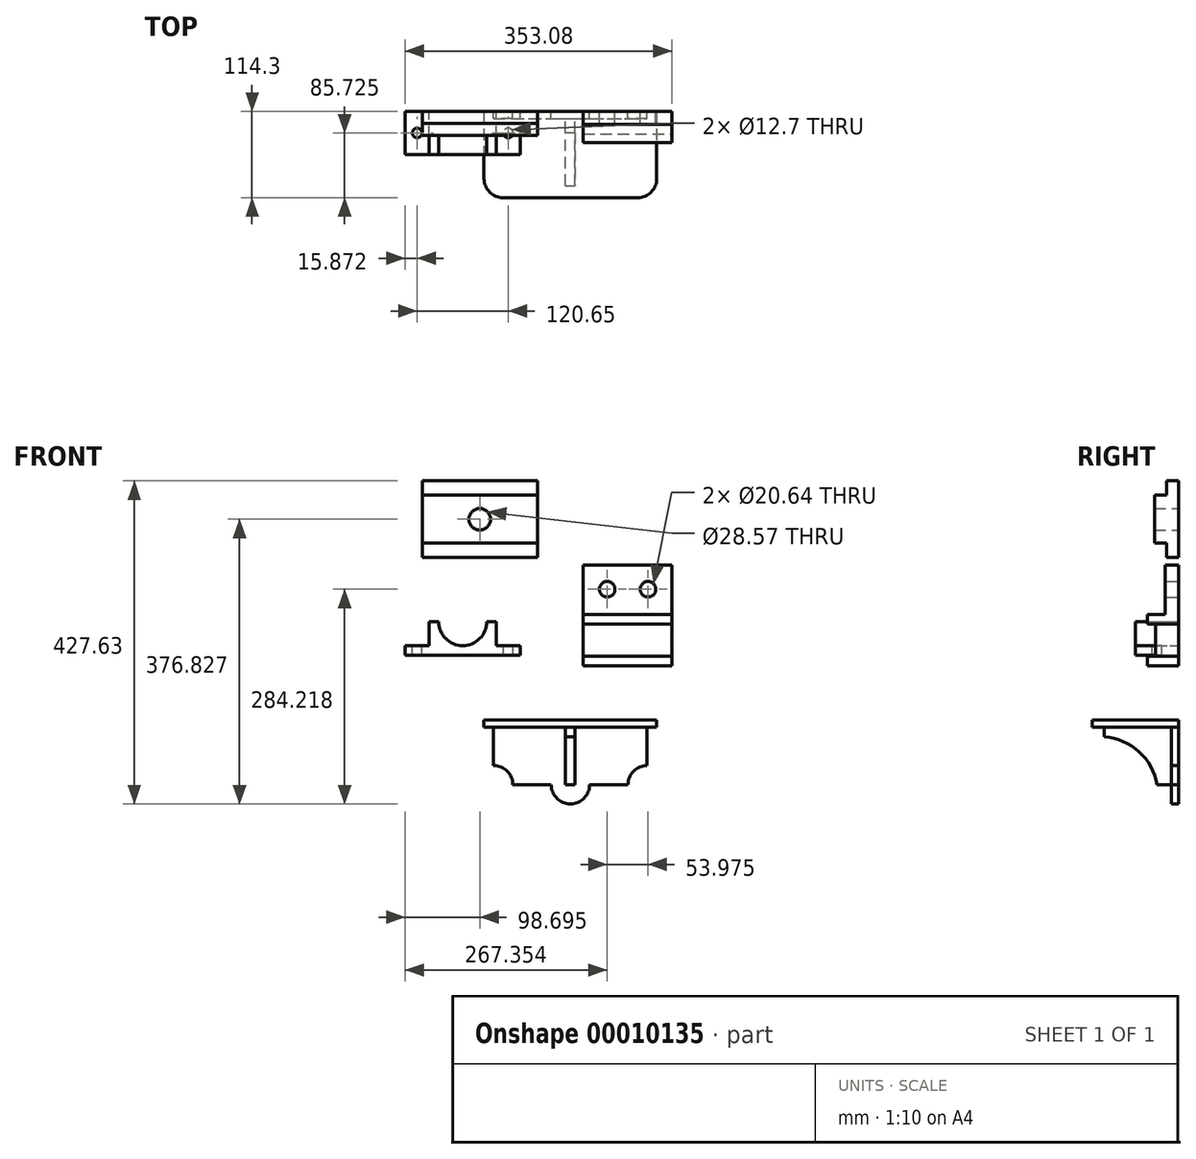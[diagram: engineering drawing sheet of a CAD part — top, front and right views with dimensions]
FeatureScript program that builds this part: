
annotation { "Feature Type Name" : "Feature", "Feature Type Description" : "" }
export const myFeature = defineFeature(function(context is Context, id is Id, definition is map)
    precondition{}
    {
        {
            var Q0;
            Q0=qCreatedBy(makeId("Front.planeOp"),FACE);
            var sketch = newSketch(context, id + "F0", { "sketchPlane" : qUnion([Q0])});
            skLineSegment(sketch, "E0.bottom", {"start": v(-212.65, 155.92) * mm, "end": v(-60.25, 155.92) * mm});
            skLineSegment(sketch, "E0.top", {"start": v(-212.65, 54.32) * mm, "end": v(-60.25, 54.32) * mm});
            skLineSegment(sketch, "E0.left", {"start": v(-212.65, 155.92) * mm, "end": v(-212.65, 54.32) * mm});
            skLineSegment(sketch, "E0.right", {"start": v(-60.25, 155.92) * mm, "end": v(-60.25, 54.32) * mm});
            skLineSegment(sketch, "E1", {"start": v(-212.65, 73.37) * mm, "end": v(-60.25, 73.37) * mm});
            skLineSegment(sketch, "E2", {"start": v(-212.65, 136.87) * mm, "end": v(-60.25, 136.87) * mm});
            skLineSegment(sketch, "E3", {"start": v(-212.65, 105.12) * mm, "end": v(-60.25, 105.12) * mm});
            skLineSegment(sketch, "E4", {"start": v(-136.45, 155.92) * mm, "end": v(-136.45, 54.32) * mm});
            skCircle(sketch, "E5", {"center": v(-136.45, 105.12) * mm, "radius": 14.29 * mm});
            skPoint(sketch, "E6", {"position": v(-130.17, 117.95) * mm});
            skSolve(sketch);
        }
        {
            var Q0;
            {var subQ5=sQuery(id+"F0.wireOp",EDGE,"E0.left");var subQ7=sQuery(id+"F0.wireOp",EDGE,"E2");var subQ9=makeQuery(id+"F0.imprint","INTERSECT",VERTEX,{"derivedFrom":[subQ5,subQ7]});Q0=makeQuery(id+"F0.imprint","IMPRINT",FACE,{"disambiguationData":[TD([[makeQuery(id+"F0.imprint","IMPRINT",EDGE,{"disambiguationData":[TD([[subQ9,-1.0]])],"derivedFrom":subQ5}),1.0]])]});}
            var Q1;
            {var subQ5=sQuery(id+"F0.wireOp",EDGE,"E2");var subQ7=sQuery(id+"F0.wireOp",EDGE,"E0.right");var subQ9=makeQuery(id+"F0.imprint","INTERSECT",VERTEX,{"derivedFrom":[subQ7,subQ5]});Q1=makeQuery(id+"F0.imprint","IMPRINT",FACE,{"disambiguationData":[TD([[makeQuery(id+"F0.imprint","IMPRINT",EDGE,{"disambiguationData":[TD([[subQ9,-1.0]])],"derivedFrom":subQ7}),-1.0]])]});}
            var Q2;
            {var subQ5=sQuery(id+"F0.wireOp",EDGE,"E1");var subQ7=sQuery(id+"F0.wireOp",EDGE,"E0.right");var subQ9=makeQuery(id+"F0.imprint","INTERSECT",VERTEX,{"derivedFrom":[subQ7,subQ5]});Q2=makeQuery(id+"F0.imprint","IMPRINT",FACE,{"disambiguationData":[TD([[makeQuery(id+"F0.imprint","IMPRINT",EDGE,{"disambiguationData":[TD([[subQ9,1.0]])],"derivedFrom":subQ7}),-1.0]])]});}
            var Q3;
            {var subQ5=sQuery(id+"F0.wireOp",EDGE,"E1");var subQ7=sQuery(id+"F0.wireOp",EDGE,"E0.left");var subQ9=makeQuery(id+"F0.imprint","INTERSECT",VERTEX,{"derivedFrom":[subQ7,subQ5]});Q3=makeQuery(id+"F0.imprint","IMPRINT",FACE,{"disambiguationData":[TD([[makeQuery(id+"F0.imprint","IMPRINT",EDGE,{"disambiguationData":[TD([[subQ9,1.0]])],"derivedFrom":subQ7}),1.0]])]});}
            extrude(context, id + "F1", {"entities" : qUnion([Q0, Q1, Q2, Q3]), "depth" : 31.75 * mm});
        }
        {
            var Q0;
            {var subQ3=sQuery(id+"F0.wireOp",EDGE,"E0.bottom");var subQ5=sQuery(id+"F0.wireOp",EDGE,"E0.left");var subQ7=makeQuery(id+"F0.imprint","INTERSECT",VERTEX,{"derivedFrom":[subQ3,subQ5]});Q0=makeQuery(id+"F0.imprint","IMPRINT",FACE,{"disambiguationData":[TD([[makeQuery(id+"F0.imprint","IMPRINT",EDGE,{"disambiguationData":[TD([[subQ7,-1.0]])],"derivedFrom":subQ3}),-1.0]])]});}
            var Q1;
            {var subQ3=sQuery(id+"F0.wireOp",EDGE,"E0.bottom");var subQ5=sQuery(id+"F0.wireOp",EDGE,"E0.right");var subQ7=makeQuery(id+"F0.imprint","INTERSECT",VERTEX,{"derivedFrom":[subQ3,subQ5]});Q1=makeQuery(id+"F0.imprint","IMPRINT",FACE,{"disambiguationData":[TD([[makeQuery(id+"F0.imprint","IMPRINT",EDGE,{"disambiguationData":[TD([[subQ7,1.0]])],"derivedFrom":subQ3}),-1.0]])]});}
            var Q2;
            {var subQ3=sQuery(id+"F0.wireOp",EDGE,"E0.top");var subQ5=sQuery(id+"F0.wireOp",EDGE,"E0.left");var subQ7=makeQuery(id+"F0.imprint","INTERSECT",VERTEX,{"derivedFrom":[subQ3,subQ5]});Q2=makeQuery(id+"F0.imprint","IMPRINT",FACE,{"disambiguationData":[TD([[makeQuery(id+"F0.imprint","IMPRINT",EDGE,{"disambiguationData":[TD([[subQ7,-1.0]])],"derivedFrom":subQ3}),1.0]])]});}
            var Q3;
            {var subQ3=sQuery(id+"F0.wireOp",EDGE,"E0.top");var subQ5=sQuery(id+"F0.wireOp",EDGE,"E0.right");var subQ7=makeQuery(id+"F0.imprint","INTERSECT",VERTEX,{"derivedFrom":[subQ3,subQ5]});Q3=makeQuery(id+"F0.imprint","IMPRINT",FACE,{"disambiguationData":[TD([[makeQuery(id+"F0.imprint","IMPRINT",EDGE,{"disambiguationData":[TD([[subQ7,1.0]])],"derivedFrom":subQ3}),1.0]])]});}
            extrude(context, id + "F2", {"entities" : qUnion([Q0, Q1, Q2, Q3]), "operationType" : NewBodyOperationType.ADD, "depth" : 15.88 * mm});
        }
        {
            var Q0;
            Q0=qCreatedBy(makeId("Front.planeOp"),FACE);
            var sketch = newSketch(context, id + "F3", { "sketchPlane" : qUnion([Q0])});
            skLineSegment(sketch, "E7.bottom", {"start": v(0.46, 44.26) * mm, "end": v(117.94, 44.26) * mm});
            skLineSegment(sketch, "E7.top", {"start": v(0.46, -89.1) * mm, "end": v(117.94, -89.1) * mm});
            skLineSegment(sketch, "E7.left", {"start": v(0.46, 44.26) * mm, "end": v(0.46, -89.1) * mm});
            skLineSegment(sketch, "E7.right", {"start": v(117.94, 44.26) * mm, "end": v(117.94, -89.1) * mm});
            skLineSegment(sketch, "E8", {"start": v(0.46, -76.4) * mm, "end": v(117.94, -76.4) * mm});
            skLineSegment(sketch, "E9", {"start": v(0.46, -33.53) * mm, "end": v(117.94, -33.53) * mm});
            skLineSegment(sketch, "E10", {"start": v(0.46, -20.83) * mm, "end": v(117.94, -20.83) * mm});
            skPoint(sketch, "E11", {"position": v(32.21, 44.26) * mm});
            skCircle(sketch, "E12", {"center": v(32.21, 12.5) * mm, "radius": 10.32 * mm});
            skPoint(sketch, "E13", {"position": v(25.4, 20.25) * mm});
            skPoint(sketch, "E14", {"position": v(86.19, 44.26) * mm});
            skCircle(sketch, "E15", {"center": v(86.19, 12.5) * mm, "radius": 10.32 * mm});
            skPoint(sketch, "E16", {"position": v(78.47, 19.36) * mm});
            skSolve(sketch);
        }
        {
            var Q0;
            {var subQ2=sQuery(id+"F3.wireOp",EDGE,"E7.bottom");Q0=makeQuery(id+"F3.imprint","IMPRINT",FACE,{"disambiguationData":[TD([[makeQuery(id+"F3.imprint","IMPRINT",EDGE,{"derivedFrom":subQ2}),-1.0]])]});}
            extrude(context, id + "F4", {"entities" : qUnion([Q0]), "depth" : 17.46 * mm});
        }
        {
            var Q0;
            {var subQ1=sQuery(id+"F3.wireOp",EDGE,"E9");Q0=makeQuery(id+"F3.imprint","IMPRINT",FACE,{"disambiguationData":[TD([[makeQuery(id+"F3.imprint","IMPRINT",EDGE,{"derivedFrom":subQ1}),1.0]])]});}
            var Q1;
            {var subQ2=sQuery(id+"F3.wireOp",EDGE,"E7.top");Q1=makeQuery(id+"F3.imprint","IMPRINT",FACE,{"disambiguationData":[TD([[makeQuery(id+"F3.imprint","IMPRINT",EDGE,{"derivedFrom":subQ2}),1.0]])]});}
            extrude(context, id + "F5", {"entities" : qUnion([Q0, Q1]), "operationType" : NewBodyOperationType.ADD, "depth" : 41.27 * mm});
        }
        {
            var Q0;
            {var subQ1=sQuery(id+"F3.wireOp",EDGE,"E8");Q0=makeQuery(id+"F3.imprint","IMPRINT",FACE,{"disambiguationData":[TD([[makeQuery(id+"F3.imprint","IMPRINT",EDGE,{"derivedFrom":subQ1}),1.0]])]});}
            extrude(context, id + "F6", {"entities" : qUnion([Q0]), "depth" : 30.16 * mm});
        }
        {
            var Q0;
            Q0=qCreatedBy(makeId("Front.planeOp"),FACE);
            var sketch = newSketch(context, id + "F7", { "sketchPlane" : qUnion([Q0])});
            skLineSegment(sketch, "E17.right", {"start": v(-82.74, -62.08) * mm, "end": v(-82.74, -74.78) * mm});
            skPoint(sketch, "E18", {"position": v(-82.74, -62.08) * mm});
            skLineSegment(sketch, "E19", {"start": v(-82.74, -62.08) * mm, "end": v(-114.5, -62.08) * mm});
            skLineSegment(sketch, "E20", {"start": v(-114.5, -62.08) * mm, "end": v(-114.5, -30.33) * mm});
            skLineSegment(sketch, "E21", {"start": v(-158.94, -62.08) * mm, "end": v(-158.94, -74.78) * mm});
            skLineSegment(sketch, "E22", {"start": v(-127.2, -30.33) * mm, "end": v(-114.5, -30.33) * mm});
            skLineSegment(sketch, "E23", {"start": v(-82.74, -74.78) * mm, "end": v(-158.94, -74.78) * mm});
            skArc(sketch, "E24", {"start": v(-158.94, -62.08) * mm, "mid": v(-136.5, -52.78) * mm, "end": v(-127.2, -30.33) * mm});
            skPoint(sketch, "E25", {"position": v(-137.5, -53.74) * mm});
            skLineSegment(sketch, "E26.0.MirrorCS", {"start": v(-190.7, -30.33) * mm, "end": v(-203.4, -30.33) * mm});
            skLineSegment(sketch, "E26.1.MirrorCS", {"start": v(-235.14, -74.78) * mm, "end": v(-158.94, -74.78) * mm});
            skPoint(sketch, "E26.2.MirrorP", {"position": v(-235.14, -62.08) * mm});
            skLineSegment(sketch, "E26.3.MirrorCS", {"start": v(-235.14, -62.08) * mm, "end": v(-203.4, -62.08) * mm});
            skPoint(sketch, "E26.4.MirrorP", {"position": v(-180.4, -53.74) * mm});
            skArc(sketch, "E26.5.MirrorCS", {"start": v(-158.94, -62.08) * mm, "mid": v(-181.4, -52.78) * mm, "end": v(-190.7, -30.33) * mm});
            skLineSegment(sketch, "E26.6.MirrorCS", {"start": v(-235.14, -62.08) * mm, "end": v(-235.14, -74.78) * mm});
            skLineSegment(sketch, "E26.7.MirrorCS", {"start": v(-203.4, -62.08) * mm, "end": v(-203.4, -30.33) * mm});
            skSolve(sketch);
        }
        {
            var Q0;
            Q0=makeQuery(id+"F7.imprint","IMPRINT",FACE,{"disambiguationData":[TD([[makeQuery(id+"F7.imprint","IMPRINT",EDGE,{"derivedFrom":sQuery(id+"F7.wireOp",EDGE,"E17.right")}),-1.0]])]});
            var Q1;
            Q1=makeQuery(id+"F7.imprint","IMPRINT",FACE,{"disambiguationData":[TD([[makeQuery(id+"F7.imprint","IMPRINT",EDGE,{"derivedFrom":sQuery(id+"F7.wireOp",EDGE,"E21")}),-1.0]])]});
            extrude(context, id + "F8", {"entities" : qUnion([Q0, Q1]), "depth" : 57.15 * mm});
        }
        {
            var Q0;
            Q0=makeQuery(id+"F8.opExtrude","SWEPT_FACE",FACE,{"disambiguationData":[OSD([sQuery(id+"F7.wireOp",EDGE,"E26.3.MirrorCS")])]});
            var sketch = newSketch(context, id + "F9", { "sketchPlane" : qUnion([Q0])});
            skPoint(sketch, "E27", {"position": v(-235.14, -28.58) * mm});
            skLineSegment(sketch, "E28", {"start": v(-235.14, -28.58) * mm, "end": v(-219.27, -28.58) * mm});
            skCircle(sketch, "E29", {"center": v(-219.27, -28.58) * mm, "radius": 6.35 * mm});
            skPoint(sketch, "E30", {"position": v(-214.3, -32.53) * mm});
            skSolve(sketch);
        }
        {
            var Q0;
            Q0=makeQuery(id+"F8.opExtrude","SWEPT_FACE",FACE,{"disambiguationData":[OSD([sQuery(id+"F7.wireOp",EDGE,"E19")])]});
            var sketch = newSketch(context, id + "F10", { "sketchPlane" : qUnion([Q0])});
            skLineSegment(sketch, "E31", {"start": v(-82.74, -28.58) * mm, "end": v(-98.62, -28.58) * mm});
            skCircle(sketch, "E32", {"center": v(-98.62, -28.58) * mm, "radius": 6.35 * mm});
            skPoint(sketch, "E33", {"position": v(-103.7, -24.77) * mm});
            skSolve(sketch);
        }
        {
            var Q0;
            Q0=makeQuery(id+"F10.imprint","IMPRINT",FACE,{"disambiguationData":[TD([[makeQuery(id+"F10.imprint","IMPRINT",EDGE,{"derivedFrom":sQuery(id+"F10.wireOp",EDGE,"E32")}),1.0]])]});
            extrude(context, id + "F11", {"entities" : qUnion([Q0]), "operationType" : NewBodyOperationType.REMOVE, "oppositeDirection" : true, "depth" : 12.7 * mm});
        }
        {
            var Q0;
            Q0 = qSketchRegion(id + "F9", true);
            extrude(context, id + "F12", {"entities" : qUnion([Q0]), "operationType" : NewBodyOperationType.REMOVE, "oppositeDirection" : true, "depth" : 12.7 * mm});
        }
        {
            var Q0;
            Q0=qCreatedBy(makeId("Front.planeOp"),FACE);
            var sketch = newSketch(context, id + "F13", { "sketchPlane" : qUnion([Q0])});
            skLineSegment(sketch, "E34.bottom", {"start": v(-118.05, -170.11) * mm, "end": v(85.15, -170.11) * mm});
            skLineSegment(sketch, "E34.left", {"start": v(-118.05, -170.11) * mm, "end": v(-118.05, -220.91) * mm});
            skLineSegment(sketch, "E34.right", {"start": v(85.15, -170.11) * mm, "end": v(85.15, -220.91) * mm});
            skArc(sketch, "E35", {"start": v(-92.65, -246.31) * mm, "mid": v(-100.1, -228.35) * mm, "end": v(-118.05, -220.91) * mm});
            skArc(sketch, "E36", {"start": v(85.15, -220.91) * mm, "mid": v(67.19, -228.35) * mm, "end": v(59.75, -246.31) * mm});
            skPoint(sketch, "E37", {"position": v(-97.01, -232.08) * mm});
            skPoint(sketch, "E38", {"position": v(62.7, -234.41) * mm});
            skLineSegment(sketch, "E39", {"start": v(-92.65, -246.31) * mm, "end": v(-41.85, -246.31) * mm});
            skArc(sketch, "E40", {"start": v(-41.85, -246.31) * mm, "mid": v(-16.45, -271.71) * mm, "end": v(8.95, -246.31) * mm});
            skPoint(sketch, "E41", {"position": v(3.99, -261.39) * mm});
            skLineSegment(sketch, "E42.trimOffspring", {"start": v(8.95, -246.31) * mm, "end": v(59.75, -246.31) * mm});
            skPoint(sketch, "E43", {"position": v(-22.8, -246.31) * mm});
            skPoint(sketch, "E44", {"position": v(-10.1, -246.31) * mm});
            skLineSegment(sketch, "E45.bottom", {"start": v(-22.8, -246.31) * mm, "end": v(-10.1, -246.31) * mm});
            skLineSegment(sketch, "E45.top", {"start": v(-22.8, -170.11) * mm, "end": v(-10.1, -170.11) * mm});
            skLineSegment(sketch, "E45.left", {"start": v(-22.8, -246.31) * mm, "end": v(-22.8, -170.11) * mm});
            skLineSegment(sketch, "E45.right", {"start": v(-10.1, -246.31) * mm, "end": v(-10.1, -170.11) * mm});
            skSolve(sketch);
        }
        {
            var Q0;
            {var subQ3=sQuery(id+"F13.wireOp",EDGE,"E34.left");Q0=makeQuery(id+"F13.imprint","IMPRINT",FACE,{"disambiguationData":[TD([[makeQuery(id+"F13.imprint","IMPRINT",EDGE,{"derivedFrom":subQ3}),1.0]])]});}
            extrude(context, id + "F14", {"entities" : qUnion([Q0]), "depth" : 9.52 * mm});
        }
        {
            var Q0;
            Q0=makeQuery(id+"F13.imprint","IMPRINT",FACE,{"disambiguationData":[TD([[makeQuery(id+"F13.imprint","IMPRINT",EDGE,{"derivedFrom":sQuery(id+"F13.wireOp",EDGE,"E45.bottom")}),1.0]])]});
            extrude(context, id + "F15", {"entities" : qUnion([Q0]), "operationType" : NewBodyOperationType.ADD, "depth" : 98.42 * mm});
        }
        {
            var Q0;
            Q0=makeQuery(id+"F15.opExtrude","SWEPT_FACE",FACE,{"disambiguationData":[OSD([sQuery(id+"F13.wireOp",EDGE,"E45.right")])]});
            var sketch = newSketch(context, id + "F16", { "sketchPlane" : qUnion([Q0])});
            skPoint(sketch, "E46", {"position": v(-98.43, -182.81) * mm});
            skPoint(sketch, "E47", {"position": v(-28.58, -246.31) * mm});
            skPoint(sketch, "E48", {"position": v(-98.43, -170.11) * mm});
            skPoint(sketch, "E49", {"position": v(-48.02, -189.17) * mm});
            skPoint(sketch, "E50", {"position": v(-9.53, -246.31) * mm});
            skCircle(sketch, "E51", {"center": v(-103.4, -259.05) * mm, "radius": 76.2 * mm});
            skSolve(sketch);
        }
        {
            var Q0;
            {var subQ0=sQuery(id+"F13.wireOp",EDGE,"E34.bottom");var subQ1=sQuery(id+"F13.wireOp",EDGE,"E45.top");Q0=makeQuery(id+"F15.boolean.opBoolean","MERGE",FACE,{"derivedFrom":[makeQuery(id+"F14.opExtrude","SWEPT_FACE",FACE,{"disambiguationData":[OSD([subQ0]),TDD([makeQuery(id+"F13.imprint","IMPRINT",EDGE,{"disambiguationData":[TD([[makeQuery(id+"F13.imprint","INTERSECT",VERTEX,{"derivedFrom":[subQ0,sQuery(id+"F13.wireOp",EDGE,"E34.left")]}),-1.0]])],"derivedFrom":subQ0})])]}),makeQuery(id+"F14.opExtrude","SWEPT_FACE",FACE,{"disambiguationData":[OSD([subQ0]),TDD([makeQuery(id+"F13.imprint","IMPRINT",EDGE,{"disambiguationData":[TD([[makeQuery(id+"F13.imprint","INTERSECT",VERTEX,{"derivedFrom":[subQ0,sQuery(id+"F13.wireOp",EDGE,"E34.right")]}),1.0]])],"derivedFrom":subQ0})])]}),makeQuery(id+"F15.opExtrude","SWEPT_FACE",FACE,{"disambiguationData":[OSD([subQ1])]})]});}
            var sketch = newSketch(context, id + "F17", { "sketchPlane" : qUnion([Q0])});
            skLineSegment(sketch, "E52", {"start": v(-118.05, 0) * mm, "end": v(-130.75, 0) * mm});
            skLineSegment(sketch, "E53", {"start": v(-130.75, 0) * mm, "end": v(97.85, 0) * mm});
            skLineSegment(sketch, "E54", {"start": v(-130.75, 0) * mm, "end": v(-130.75, -88.9) * mm});
            skLineSegment(sketch, "E55", {"start": v(-105.35, -114.3) * mm, "end": v(72.45, -114.3) * mm});
            skLineSegment(sketch, "E56", {"start": v(97.85, 0) * mm, "end": v(97.85, -88.9) * mm});
            skPoint(sketch, "E57.visualSharp", {"position": v(-130.75, -114.3) * mm});
            skArc(sketch, "E57.filletArc", {"start": v(-130.75, -88.9) * mm, "mid": v(-123.31, -106.86) * mm, "end": v(-105.35, -114.3) * mm});
            skPoint(sketch, "E58.visualSharp", {"position": v(97.85, -114.3) * mm});
            skArc(sketch, "E58.filletArc", {"start": v(72.45, -114.3) * mm, "mid": v(90.4, -106.86) * mm, "end": v(97.85, -88.9) * mm});
            skSolve(sketch);
        }
        {
            var Q0;
            Q0 = qSketchRegion(id + "F17", true);
            extrude(context, id + "F18", {"entities" : qUnion([Q0]), "operationType" : NewBodyOperationType.ADD, "depth" : 9.52 * mm});
        }
        {
            var Q0;
            {var subQ0=sQuery(id+"F13.wireOp",EDGE,"E45.right");var subQ2=sQuery(id+"F16.wireOp",EDGE,"E51");var subQ4=makeQuery(id+"F15.opExtrude","CAP_EDGE",EDGE,{"disambiguationData":[OSD([subQ0])],"isStart":false});var subQ6=makeQuery(id+"F16.imprint","INTERSECT",VERTEX,{"derivedFrom":[subQ4,subQ2]});Q0=makeQuery(id+"F16.imprint","IMPRINT",FACE,{"disambiguationData":[TD([[makeQuery(id+"F16.imprint","IMPRINT",EDGE,{"disambiguationData":[TD([[subQ6,1.0]])],"derivedFrom":subQ2}),1.0]])]});}
            var Q1;
            {var subQ0=sQuery(id+"F13.wireOp",EDGE,"E45.right");var subQ2=sQuery(id+"F16.wireOp",EDGE,"E51");var subQ4=makeQuery(id+"F15.opExtrude","CAP_EDGE",EDGE,{"disambiguationData":[OSD([subQ0])],"isStart":false});var subQ6=makeQuery(id+"F16.imprint","INTERSECT",VERTEX,{"derivedFrom":[subQ4,subQ2]});Q1=makeQuery(id+"F16.imprint","IMPRINT",FACE,{"disambiguationData":[TD([[makeQuery(id+"F16.imprint","IMPRINT",EDGE,{"disambiguationData":[TD([[subQ6,-1.0]])],"derivedFrom":subQ2}),1.0]])]});}
            extrude(context, id + "F19", {"entities" : qUnion([Q0, Q1]), "operationType" : NewBodyOperationType.REMOVE, "oppositeDirection" : true, "depth" : 25.4 * mm});
        }
    });
